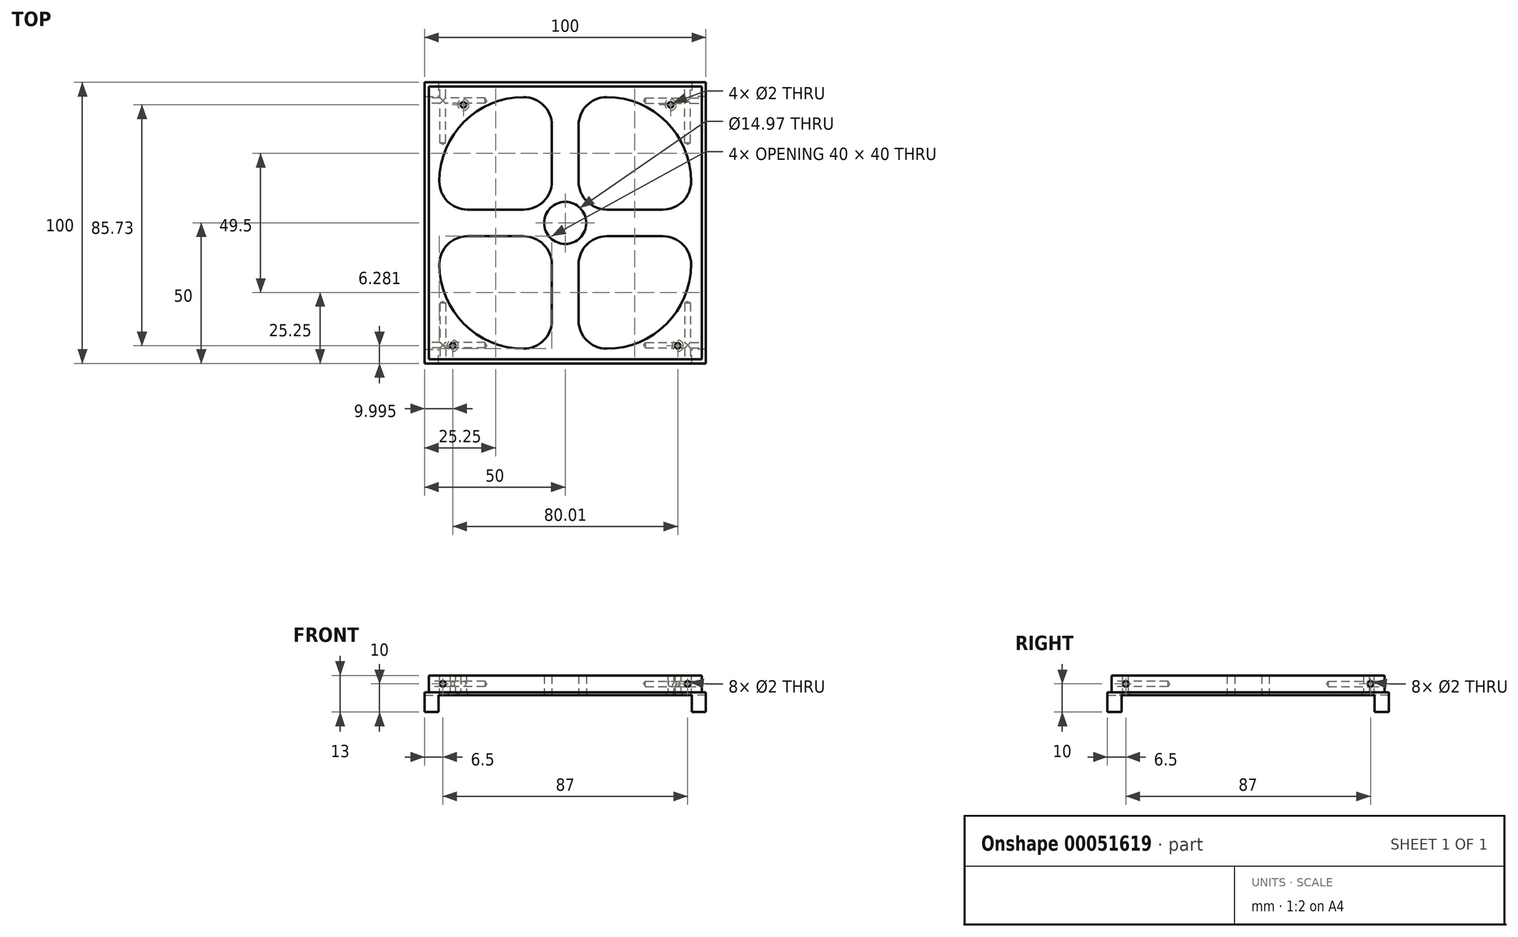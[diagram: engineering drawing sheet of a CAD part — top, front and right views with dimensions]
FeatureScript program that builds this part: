
annotation { "Feature Type Name" : "Feature", "Feature Type Description" : "" }
export const myFeature = defineFeature(function(context is Context, id is Id, definition is map)
    precondition{}
    {
        {
            var Q0;
            Q0=qCreatedBy(makeId("Top.planeOp"),FACE);
            var sketch = newSketch(context, id + "F0", { "sketchPlane" : qUnion([Q0])});
            skLineSegment(sketch, "E0.rect.bottom", {"start": v(-50, 50) * mm, "end": v(50, 50) * mm});
            skLineSegment(sketch, "E0.rect.top", {"start": v(-50, -50) * mm, "end": v(50, -50) * mm});
            skLineSegment(sketch, "E0.rect.left", {"start": v(-50, 50) * mm, "end": v(-50, -50) * mm});
            skLineSegment(sketch, "E0.rect.right", {"start": v(50, 50) * mm, "end": v(50, -50) * mm});
            skPoint(sketch, "E0.rect.middle", {"position": v(0, 0) * mm});
            skLineSegment(sketch, "E1.rect.bottom", {"start": v(-48.5, 48.5) * mm, "end": v(48.5, 48.5) * mm});
            skLineSegment(sketch, "E1.rect.top", {"start": v(-48.5, -48.5) * mm, "end": v(48.5, -48.5) * mm});
            skLineSegment(sketch, "E1.rect.left", {"start": v(-48.5, 48.5) * mm, "end": v(-48.5, -48.5) * mm});
            skLineSegment(sketch, "E1.rect.right", {"start": v(48.5, 48.5) * mm, "end": v(48.5, -48.5) * mm});
            skLineSegment(sketch, "E2.rect.bottom", {"start": v(-14.75, 4.75) * mm, "end": v(-34.75, 4.75) * mm});
            skLineSegment(sketch, "E2.rect.top", {"start": v(-14.75, 44.75) * mm, "end": v(-14.75, 44.75) * mm});
            skLineSegment(sketch, "E2.rect.left", {"start": v(-4.75, 14.75) * mm, "end": v(-4.75, 34.75) * mm});
            skLineSegment(sketch, "E2.rect.right", {"start": v(-44.75, 14.75) * mm, "end": v(-44.75, 14.75) * mm});
            skPoint(sketch, "E2.rect.middle", {"position": v(-24.75, 24.75) * mm});
            skPoint(sketch, "E3.visualSharp", {"position": v(-44.75, 44.75) * mm});
            skArc(sketch, "E3.filletArc", {"start": v(-14.75, 44.75) * mm, "mid": v(-35.96, 35.96) * mm, "end": v(-44.75, 14.75) * mm});
            skPoint(sketch, "E4.visualSharp", {"position": v(-4.75, 44.75) * mm});
            skArc(sketch, "E4.filletArc", {"start": v(-4.75, 34.75) * mm, "mid": v(-7.68, 41.82) * mm, "end": v(-14.75, 44.75) * mm});
            skPoint(sketch, "E5.visualSharp", {"position": v(-4.75, 4.75) * mm});
            skArc(sketch, "E5.filletArc", {"start": v(-14.75, 4.75) * mm, "mid": v(-7.68, 7.68) * mm, "end": v(-4.75, 14.75) * mm});
            skPoint(sketch, "E6.visualSharp", {"position": v(-44.75, 4.75) * mm});
            skArc(sketch, "E6.filletArc", {"start": v(-44.75, 14.75) * mm, "mid": v(-41.82, 7.68) * mm, "end": v(-34.75, 4.75) * mm});
            skLineSegment(sketch, "E7.MirrorCS", {"start": v(4.75, 14.75) * mm, "end": v(4.75, 34.75) * mm});
            skArc(sketch, "E8.MirrorCS", {"start": v(4.75, 34.75) * mm, "mid": v(7.68, 41.82) * mm, "end": v(14.75, 44.75) * mm});
            skLineSegment(sketch, "E9.MirrorCS", {"start": v(14.75, 44.75) * mm, "end": v(14.75, 44.75) * mm});
            skArc(sketch, "E10.MirrorCS", {"start": v(14.75, 44.75) * mm, "mid": v(35.96, 35.96) * mm, "end": v(44.75, 14.75) * mm});
            skLineSegment(sketch, "E11.MirrorCS", {"start": v(44.75, 14.75) * mm, "end": v(44.75, 14.75) * mm});
            skArc(sketch, "E12.MirrorCS", {"start": v(44.75, 14.75) * mm, "mid": v(41.82, 7.68) * mm, "end": v(34.75, 4.75) * mm});
            skLineSegment(sketch, "E13.MirrorCS", {"start": v(14.75, 4.75) * mm, "end": v(34.75, 4.75) * mm});
            skArc(sketch, "E14.MirrorCS", {"start": v(14.75, 4.75) * mm, "mid": v(7.68, 7.68) * mm, "end": v(4.75, 14.75) * mm});
            skPoint(sketch, "E15.MirrorP", {"position": v(24.75, 24.75) * mm});
            skArc(sketch, "E16.MirrorCS", {"start": v(14.75, -4.75) * mm, "mid": v(7.68, -7.68) * mm, "end": v(4.75, -14.75) * mm});
            skLineSegment(sketch, "E17.MirrorCS", {"start": v(4.75, -14.75) * mm, "end": v(4.75, -34.75) * mm});
            skArc(sketch, "E18.MirrorCS", {"start": v(4.75, -34.75) * mm, "mid": v(7.68, -41.82) * mm, "end": v(14.75, -44.75) * mm});
            skLineSegment(sketch, "E19.MirrorCS", {"start": v(14.75, -44.75) * mm, "end": v(14.75, -44.75) * mm});
            skArc(sketch, "E20.MirrorCS", {"start": v(14.75, -44.75) * mm, "mid": v(35.96, -35.96) * mm, "end": v(44.75, -14.75) * mm});
            skLineSegment(sketch, "E21.MirrorCS", {"start": v(44.75, -14.75) * mm, "end": v(44.75, -14.75) * mm});
            skArc(sketch, "E22.MirrorCS", {"start": v(44.75, -14.75) * mm, "mid": v(41.82, -7.68) * mm, "end": v(34.75, -4.75) * mm});
            skLineSegment(sketch, "E23.MirrorCS", {"start": v(14.75, -4.75) * mm, "end": v(34.75, -4.75) * mm});
            skPoint(sketch, "E24.MirrorP", {"position": v(24.75, -24.75) * mm});
            skLineSegment(sketch, "E25.MirrorCS", {"start": v(-4.75, -14.75) * mm, "end": v(-4.75, -34.75) * mm});
            skArc(sketch, "E26.MirrorCS", {"start": v(-14.75, -4.75) * mm, "mid": v(-7.68, -7.68) * mm, "end": v(-4.75, -14.75) * mm});
            skLineSegment(sketch, "E27.MirrorCS", {"start": v(-14.75, -4.75) * mm, "end": v(-34.75, -4.75) * mm});
            skArc(sketch, "E28.MirrorCS", {"start": v(-44.75, -14.75) * mm, "mid": v(-41.82, -7.68) * mm, "end": v(-34.75, -4.75) * mm});
            skLineSegment(sketch, "E29.MirrorCS", {"start": v(-44.75, -14.75) * mm, "end": v(-44.75, -14.75) * mm});
            skArc(sketch, "E30.MirrorCS", {"start": v(-14.75, -44.75) * mm, "mid": v(-35.96, -35.96) * mm, "end": v(-44.75, -14.75) * mm});
            skLineSegment(sketch, "E31.MirrorCS", {"start": v(-14.75, -44.75) * mm, "end": v(-14.75, -44.75) * mm});
            skArc(sketch, "E32.MirrorCS", {"start": v(-4.75, -34.75) * mm, "mid": v(-7.68, -41.82) * mm, "end": v(-14.75, -44.75) * mm});
            skPoint(sketch, "E33.MirrorP", {"position": v(-24.75, -24.75) * mm});
            skPoint(sketch, "E34", {"position": v(42.5, -42.5) * mm});
            skPoint(sketch, "E35.MirrorP", {"position": v(-42.5, -42.5) * mm});
            skPoint(sketch, "E36.MirrorP", {"position": v(42.5, 42.5) * mm});
            skPoint(sketch, "E37.MirrorP", {"position": v(-42.5, 42.5) * mm});
            skCircle(sketch, "E38", {"center": v(0, 0) * mm, "radius": 7.48 * mm});
            skSolve(sketch);
        }
        {
            var Q0;
            Q0=makeQuery(id+"F0.imprint","IMPRINT",FACE,{"disambiguationData":[TD([[makeQuery(id+"F0.imprint","IMPRINT",EDGE,{"derivedFrom":sQuery(id+"F0.wireOp",EDGE,"E1.rect.bottom")}),-1.0]])]});
            extrude(context, id + "F1", {"entities" : qUnion([Q0]), "depth" : 6 * mm});
        }
        {
            var Q0;
            Q0=qSketchRegion(id+"F0",true);
            var Q1;
            Q1=makeQuery(id+"F1.opExtrude","CAP_FACE",FACE,{"disambiguationData":[OSD([sQuery(id+"F0.wireOp",EDGE,"E1.rect.bottom"),sQuery(id+"F0.wireOp",EDGE,"E1.rect.top"),sQuery(id+"F0.wireOp",EDGE,"E1.rect.left"),sQuery(id+"F0.wireOp",EDGE,"E1.rect.right"),sQuery(id+"F0.wireOp",EDGE,"E2.rect.bottom"),sQuery(id+"F0.wireOp",EDGE,"E2.rect.top"),sQuery(id+"F0.wireOp",EDGE,"E2.rect.left"),sQuery(id+"F0.wireOp",EDGE,"E2.rect.right"),sQuery(id+"F0.wireOp",EDGE,"d764ca65-7f6a-4e13-98eb-a7907a3d072d0.MirrorCS"),sQuery(id+"F0.wireOp",EDGE,"4e8c5bec-c53d-4312-8259-349e49f543fe0.MirrorCS"),sQuery(id+"F0.wireOp",EDGE,"d6a0bf7c-e4bc-484e-b3d5-183d898144500.MirrorCS"),sQuery(id+"F0.wireOp",EDGE,"45a758ec-378c-46c5-b086-a70cc1cacffd0.MirrorCS"),sQuery(id+"F0.wireOp",EDGE,"a64d5360-d78c-41ef-9f44-8c8436a09bba0.MirrorCS"),sQuery(id+"F0.wireOp",EDGE,"c998a958-b69a-464e-a296-dd7f6d349ec80.MirrorCS"),sQuery(id+"F0.wireOp",EDGE,"a4bf1b2a-a2f4-4ab3-9d73-85797b196d270.MirrorCS"),sQuery(id+"F0.wireOp",EDGE,"ecd2f3fb-4ea3-4913-80f4-94ebebe2d04e0.MirrorCS"),sQuery(id+"F0.wireOp",EDGE,"085a2cb5-2e3f-4cc3-a5b9-01c6e75669f10.MirrorCS"),sQuery(id+"F0.wireOp",EDGE,"73d67a52-dadc-4bd6-8141-d25047cb753b0.MirrorCS"),sQuery(id+"F0.wireOp",EDGE,"8f6832c0-858d-4205-8574-29f35786d1620.MirrorCS"),sQuery(id+"F0.wireOp",EDGE,"ecc9a695-4792-4055-9804-abf58933c5b20.MirrorCS")])],"isStart":false});
            extrude(context, id + "F2", {"entities" : qUnion([Q0, Q1]), "operationType" : NewBodyOperationType.ADD, "depth" : 1 * mm});
        }
        {
            var Q0;
            {var subQ0=sQuery(id+"F0.wireOp",EDGE,"E1.rect.bottom");Q0=makeQuery(id+"F2.boolean.opBoolean","MERGE",FACE,{"derivedFrom":[makeQuery(id+"F1.opExtrude","SWEPT_FACE",FACE,{"disambiguationData":[OSD([subQ0])]}),makeQuery(id+"F2.opExtrude","SWEPT_FACE",FACE,{"disambiguationData":[OSD([subQ0]),TDD([makeQuery(id+"F1.opExtrude","CAP_EDGE",EDGE,{"disambiguationData":[OSD([subQ0])],"isStart":false})])]})]});}
            var sketch = newSketch(context, id + "F3", { "sketchPlane" : qUnion([Q0])});
            skPoint(sketch, "E39", {"position": v(-43.5, 4) * mm});
            skPoint(sketch, "E40.MirrorP", {"position": v(43.5, 4) * mm});
            skSolve(sketch);
        }
        {
            var Q0;
            Q0=sQuery(id+"F3.wireOp",VERTEX,"E39");
            var Q1;
            Q1=sQuery(id+"F3.wireOp",VERTEX,"E40.MirrorP");
            var Q2;
            Q2=makeQuery(id+"F1.opExtrude","SWEPT_BODY",BODY,{"disambiguationData":[OSD([sQuery(id+"F0.wireOp",EDGE,"E1.rect.bottom"),sQuery(id+"F0.wireOp",EDGE,"E1.rect.top"),sQuery(id+"F0.wireOp",EDGE,"E1.rect.left"),sQuery(id+"F0.wireOp",EDGE,"E1.rect.right"),sQuery(id+"F0.wireOp",EDGE,"E2.rect.bottom"),sQuery(id+"F0.wireOp",EDGE,"E2.rect.top"),sQuery(id+"F0.wireOp",EDGE,"E2.rect.left"),sQuery(id+"F0.wireOp",EDGE,"E2.rect.right"),sQuery(id+"F0.wireOp",EDGE,"E3.filletArc"),sQuery(id+"F0.wireOp",EDGE,"E4.filletArc"),sQuery(id+"F0.wireOp",EDGE,"E5.filletArc"),sQuery(id+"F0.wireOp",EDGE,"E6.filletArc"),sQuery(id+"F0.wireOp",EDGE,"E7.MirrorCS"),sQuery(id+"F0.wireOp",EDGE,"E8.MirrorCS"),sQuery(id+"F0.wireOp",EDGE,"E9.MirrorCS"),sQuery(id+"F0.wireOp",EDGE,"E10.MirrorCS"),sQuery(id+"F0.wireOp",EDGE,"E11.MirrorCS"),sQuery(id+"F0.wireOp",EDGE,"E12.MirrorCS"),sQuery(id+"F0.wireOp",EDGE,"E13.MirrorCS"),sQuery(id+"F0.wireOp",EDGE,"E14.MirrorCS"),sQuery(id+"F0.wireOp",EDGE,"E16.MirrorCS"),sQuery(id+"F0.wireOp",EDGE,"E17.MirrorCS"),sQuery(id+"F0.wireOp",EDGE,"E18.MirrorCS"),sQuery(id+"F0.wireOp",EDGE,"E19.MirrorCS"),sQuery(id+"F0.wireOp",EDGE,"E20.MirrorCS"),sQuery(id+"F0.wireOp",EDGE,"E21.MirrorCS"),sQuery(id+"F0.wireOp",EDGE,"E22.MirrorCS"),sQuery(id+"F0.wireOp",EDGE,"E23.MirrorCS"),sQuery(id+"F0.wireOp",EDGE,"E25.MirrorCS"),sQuery(id+"F0.wireOp",EDGE,"E26.MirrorCS"),sQuery(id+"F0.wireOp",EDGE,"E27.MirrorCS"),sQuery(id+"F0.wireOp",EDGE,"E28.MirrorCS"),sQuery(id+"F0.wireOp",EDGE,"E29.MirrorCS"),sQuery(id+"F0.wireOp",EDGE,"E30.MirrorCS"),sQuery(id+"F0.wireOp",EDGE,"E31.MirrorCS"),sQuery(id+"F0.wireOp",EDGE,"E32.MirrorCS")])]});
            hole(context, id + "F4", {"style" : HoleStyle.SIMPLE, "holeDiameter" : 2 * mm, "endStyle" : HoleEndStyle.BLIND, "holeDepth" : 20 * mm, "locations" : qUnion([Q0, Q1]), "scope" : qUnion([Q2])});
        }
        {
            var Q0;
            {var subQ0=sQuery(id+"F0.wireOp",EDGE,"E1.rect.left");Q0=makeQuery(id+"F2.boolean.opBoolean","MERGE",FACE,{"derivedFrom":[makeQuery(id+"F1.opExtrude","SWEPT_FACE",FACE,{"disambiguationData":[OSD([subQ0])]}),makeQuery(id+"F2.opExtrude","SWEPT_FACE",FACE,{"disambiguationData":[OSD([subQ0]),TDD([makeQuery(id+"F1.opExtrude","CAP_EDGE",EDGE,{"disambiguationData":[OSD([subQ0])],"isStart":false})])]})]});}
            var sketch = newSketch(context, id + "F5", { "sketchPlane" : qUnion([Q0])});
            skPoint(sketch, "E41", {"position": v(-43.5, 4) * mm});
            skPoint(sketch, "E42.MirrorP", {"position": v(43.5, 4) * mm});
            skSolve(sketch);
        }
        {
            var Q0;
            Q0=sQuery(id+"F5.wireOp",VERTEX,"E41");
            var Q1;
            Q1=sQuery(id+"F5.wireOp",VERTEX,"E42.MirrorP");
            var Q2;
            Q2=makeQuery(id+"F1.opExtrude","SWEPT_BODY",BODY,{"disambiguationData":[OSD([sQuery(id+"F0.wireOp",EDGE,"E1.rect.bottom"),sQuery(id+"F0.wireOp",EDGE,"E1.rect.top"),sQuery(id+"F0.wireOp",EDGE,"E1.rect.left"),sQuery(id+"F0.wireOp",EDGE,"E1.rect.right"),sQuery(id+"F0.wireOp",EDGE,"E2.rect.bottom"),sQuery(id+"F0.wireOp",EDGE,"E2.rect.top"),sQuery(id+"F0.wireOp",EDGE,"E2.rect.left"),sQuery(id+"F0.wireOp",EDGE,"E2.rect.right"),sQuery(id+"F0.wireOp",EDGE,"E3.filletArc"),sQuery(id+"F0.wireOp",EDGE,"E4.filletArc"),sQuery(id+"F0.wireOp",EDGE,"E5.filletArc"),sQuery(id+"F0.wireOp",EDGE,"E6.filletArc"),sQuery(id+"F0.wireOp",EDGE,"E7.MirrorCS"),sQuery(id+"F0.wireOp",EDGE,"E8.MirrorCS"),sQuery(id+"F0.wireOp",EDGE,"E9.MirrorCS"),sQuery(id+"F0.wireOp",EDGE,"E10.MirrorCS"),sQuery(id+"F0.wireOp",EDGE,"E11.MirrorCS"),sQuery(id+"F0.wireOp",EDGE,"E12.MirrorCS"),sQuery(id+"F0.wireOp",EDGE,"E13.MirrorCS"),sQuery(id+"F0.wireOp",EDGE,"E14.MirrorCS"),sQuery(id+"F0.wireOp",EDGE,"E16.MirrorCS"),sQuery(id+"F0.wireOp",EDGE,"E17.MirrorCS"),sQuery(id+"F0.wireOp",EDGE,"E18.MirrorCS"),sQuery(id+"F0.wireOp",EDGE,"E19.MirrorCS"),sQuery(id+"F0.wireOp",EDGE,"E20.MirrorCS"),sQuery(id+"F0.wireOp",EDGE,"E21.MirrorCS"),sQuery(id+"F0.wireOp",EDGE,"E22.MirrorCS"),sQuery(id+"F0.wireOp",EDGE,"E23.MirrorCS"),sQuery(id+"F0.wireOp",EDGE,"E25.MirrorCS"),sQuery(id+"F0.wireOp",EDGE,"E26.MirrorCS"),sQuery(id+"F0.wireOp",EDGE,"E27.MirrorCS"),sQuery(id+"F0.wireOp",EDGE,"E28.MirrorCS"),sQuery(id+"F0.wireOp",EDGE,"E29.MirrorCS"),sQuery(id+"F0.wireOp",EDGE,"E30.MirrorCS"),sQuery(id+"F0.wireOp",EDGE,"E31.MirrorCS"),sQuery(id+"F0.wireOp",EDGE,"E32.MirrorCS")])]});
            hole(context, id + "F6", {"style" : HoleStyle.SIMPLE, "holeDiameter" : 2 * mm, "endStyle" : HoleEndStyle.BLIND, "holeDepth" : 20 * mm, "locations" : qUnion([Q0, Q1]), "scope" : qUnion([Q2])});
        }
        {
            var Q0;
            {var subQ0=sQuery(id+"F0.wireOp",EDGE,"E1.rect.top");Q0=makeQuery(id+"F2.boolean.opBoolean","MERGE",FACE,{"derivedFrom":[makeQuery(id+"F1.opExtrude","SWEPT_FACE",FACE,{"disambiguationData":[OSD([subQ0])]}),makeQuery(id+"F2.opExtrude","SWEPT_FACE",FACE,{"disambiguationData":[OSD([subQ0]),TDD([makeQuery(id+"F1.opExtrude","CAP_EDGE",EDGE,{"disambiguationData":[OSD([subQ0])],"isStart":false})])]})]});}
            var sketch = newSketch(context, id + "F7", { "sketchPlane" : qUnion([Q0])});
            skPoint(sketch, "E43", {"position": v(-43.5, 4) * mm});
            skPoint(sketch, "E44.MirrorP", {"position": v(43.5, 4) * mm});
            skSolve(sketch);
        }
        {
            var Q0;
            Q0=sQuery(id+"F7.wireOp",VERTEX,"E43");
            var Q1;
            Q1=sQuery(id+"F7.wireOp",VERTEX,"E44.MirrorP");
            var Q2;
            Q2=makeQuery(id+"F1.opExtrude","SWEPT_BODY",BODY,{"disambiguationData":[OSD([sQuery(id+"F0.wireOp",EDGE,"E1.rect.bottom"),sQuery(id+"F0.wireOp",EDGE,"E1.rect.top"),sQuery(id+"F0.wireOp",EDGE,"E1.rect.left"),sQuery(id+"F0.wireOp",EDGE,"E1.rect.right"),sQuery(id+"F0.wireOp",EDGE,"E2.rect.bottom"),sQuery(id+"F0.wireOp",EDGE,"E2.rect.top"),sQuery(id+"F0.wireOp",EDGE,"E2.rect.left"),sQuery(id+"F0.wireOp",EDGE,"E2.rect.right"),sQuery(id+"F0.wireOp",EDGE,"E3.filletArc"),sQuery(id+"F0.wireOp",EDGE,"E4.filletArc"),sQuery(id+"F0.wireOp",EDGE,"E5.filletArc"),sQuery(id+"F0.wireOp",EDGE,"E6.filletArc"),sQuery(id+"F0.wireOp",EDGE,"E7.MirrorCS"),sQuery(id+"F0.wireOp",EDGE,"E8.MirrorCS"),sQuery(id+"F0.wireOp",EDGE,"E9.MirrorCS"),sQuery(id+"F0.wireOp",EDGE,"E10.MirrorCS"),sQuery(id+"F0.wireOp",EDGE,"E11.MirrorCS"),sQuery(id+"F0.wireOp",EDGE,"E12.MirrorCS"),sQuery(id+"F0.wireOp",EDGE,"E13.MirrorCS"),sQuery(id+"F0.wireOp",EDGE,"E14.MirrorCS"),sQuery(id+"F0.wireOp",EDGE,"E16.MirrorCS"),sQuery(id+"F0.wireOp",EDGE,"E17.MirrorCS"),sQuery(id+"F0.wireOp",EDGE,"E18.MirrorCS"),sQuery(id+"F0.wireOp",EDGE,"E19.MirrorCS"),sQuery(id+"F0.wireOp",EDGE,"E20.MirrorCS"),sQuery(id+"F0.wireOp",EDGE,"E21.MirrorCS"),sQuery(id+"F0.wireOp",EDGE,"E22.MirrorCS"),sQuery(id+"F0.wireOp",EDGE,"E23.MirrorCS"),sQuery(id+"F0.wireOp",EDGE,"E25.MirrorCS"),sQuery(id+"F0.wireOp",EDGE,"E26.MirrorCS"),sQuery(id+"F0.wireOp",EDGE,"E27.MirrorCS"),sQuery(id+"F0.wireOp",EDGE,"E28.MirrorCS"),sQuery(id+"F0.wireOp",EDGE,"E29.MirrorCS"),sQuery(id+"F0.wireOp",EDGE,"E30.MirrorCS"),sQuery(id+"F0.wireOp",EDGE,"E31.MirrorCS"),sQuery(id+"F0.wireOp",EDGE,"E32.MirrorCS")])]});
            hole(context, id + "F8", {"style" : HoleStyle.SIMPLE, "holeDiameter" : 2 * mm, "endStyle" : HoleEndStyle.BLIND, "holeDepth" : 20 * mm, "locations" : qUnion([Q0, Q1]), "scope" : qUnion([Q2])});
        }
        {
            var Q0;
            {var subQ0=sQuery(id+"F0.wireOp",EDGE,"E1.rect.right");Q0=makeQuery(id+"F2.boolean.opBoolean","MERGE",FACE,{"derivedFrom":[makeQuery(id+"F1.opExtrude","SWEPT_FACE",FACE,{"disambiguationData":[OSD([subQ0])]}),makeQuery(id+"F2.opExtrude","SWEPT_FACE",FACE,{"disambiguationData":[OSD([subQ0]),TDD([makeQuery(id+"F1.opExtrude","CAP_EDGE",EDGE,{"disambiguationData":[OSD([subQ0])],"isStart":false})])]})]});}
            var sketch = newSketch(context, id + "F9", { "sketchPlane" : qUnion([Q0])});
            skPoint(sketch, "E45", {"position": v(-43.5, 4) * mm});
            skPoint(sketch, "E46.MirrorP", {"position": v(43.5, 4) * mm});
            skSolve(sketch);
        }
        {
            var Q0;
            Q0=sQuery(id+"F9.wireOp",VERTEX,"E45");
            var Q1;
            Q1=sQuery(id+"F9.wireOp",VERTEX,"E46.MirrorP");
            var Q2;
            Q2=makeQuery(id+"F1.opExtrude","SWEPT_BODY",BODY,{"disambiguationData":[OSD([sQuery(id+"F0.wireOp",EDGE,"E1.rect.bottom"),sQuery(id+"F0.wireOp",EDGE,"E1.rect.top"),sQuery(id+"F0.wireOp",EDGE,"E1.rect.left"),sQuery(id+"F0.wireOp",EDGE,"E1.rect.right"),sQuery(id+"F0.wireOp",EDGE,"E2.rect.bottom"),sQuery(id+"F0.wireOp",EDGE,"E2.rect.top"),sQuery(id+"F0.wireOp",EDGE,"E2.rect.left"),sQuery(id+"F0.wireOp",EDGE,"E2.rect.right"),sQuery(id+"F0.wireOp",EDGE,"E3.filletArc"),sQuery(id+"F0.wireOp",EDGE,"E4.filletArc"),sQuery(id+"F0.wireOp",EDGE,"E5.filletArc"),sQuery(id+"F0.wireOp",EDGE,"E6.filletArc"),sQuery(id+"F0.wireOp",EDGE,"E7.MirrorCS"),sQuery(id+"F0.wireOp",EDGE,"E8.MirrorCS"),sQuery(id+"F0.wireOp",EDGE,"E9.MirrorCS"),sQuery(id+"F0.wireOp",EDGE,"E10.MirrorCS"),sQuery(id+"F0.wireOp",EDGE,"E11.MirrorCS"),sQuery(id+"F0.wireOp",EDGE,"E12.MirrorCS"),sQuery(id+"F0.wireOp",EDGE,"E13.MirrorCS"),sQuery(id+"F0.wireOp",EDGE,"E14.MirrorCS"),sQuery(id+"F0.wireOp",EDGE,"E16.MirrorCS"),sQuery(id+"F0.wireOp",EDGE,"E17.MirrorCS"),sQuery(id+"F0.wireOp",EDGE,"E18.MirrorCS"),sQuery(id+"F0.wireOp",EDGE,"E19.MirrorCS"),sQuery(id+"F0.wireOp",EDGE,"E20.MirrorCS"),sQuery(id+"F0.wireOp",EDGE,"E21.MirrorCS"),sQuery(id+"F0.wireOp",EDGE,"E22.MirrorCS"),sQuery(id+"F0.wireOp",EDGE,"E23.MirrorCS"),sQuery(id+"F0.wireOp",EDGE,"E25.MirrorCS"),sQuery(id+"F0.wireOp",EDGE,"E26.MirrorCS"),sQuery(id+"F0.wireOp",EDGE,"E27.MirrorCS"),sQuery(id+"F0.wireOp",EDGE,"E28.MirrorCS"),sQuery(id+"F0.wireOp",EDGE,"E29.MirrorCS"),sQuery(id+"F0.wireOp",EDGE,"E30.MirrorCS"),sQuery(id+"F0.wireOp",EDGE,"E31.MirrorCS"),sQuery(id+"F0.wireOp",EDGE,"E32.MirrorCS")])]});
            hole(context, id + "F10", {"style" : HoleStyle.SIMPLE, "holeDiameter" : 2 * mm, "endStyle" : HoleEndStyle.BLIND, "holeDepth" : 20 * mm, "locations" : qUnion([Q0, Q1]), "scope" : qUnion([Q2])});
        }
        {
            var Q0;
            {var subQ0=sQuery(id+"F0.wireOp",EDGE,"E1.rect.bottom");var subQ1=sQuery(id+"F0.wireOp",EDGE,"E1.rect.top");var subQ2=sQuery(id+"F0.wireOp",EDGE,"E1.rect.left");var subQ3=sQuery(id+"F0.wireOp",EDGE,"E1.rect.right");Q0=makeQuery(id+"F2.boolean.opBoolean","MERGE",FACE,{"derivedFrom":[makeQuery(id+"F1.opExtrude","CAP_FACE",FACE,{"disambiguationData":[OSD([subQ0,subQ1,subQ2,subQ3,sQuery(id+"F0.wireOp",EDGE,"E2.rect.bottom"),sQuery(id+"F0.wireOp",EDGE,"E2.rect.top"),sQuery(id+"F0.wireOp",EDGE,"E2.rect.left"),sQuery(id+"F0.wireOp",EDGE,"E2.rect.right"),sQuery(id+"F0.wireOp",EDGE,"E3.filletArc"),sQuery(id+"F0.wireOp",EDGE,"E4.filletArc"),sQuery(id+"F0.wireOp",EDGE,"E5.filletArc"),sQuery(id+"F0.wireOp",EDGE,"E6.filletArc"),sQuery(id+"F0.wireOp",EDGE,"E7.MirrorCS"),sQuery(id+"F0.wireOp",EDGE,"E8.MirrorCS"),sQuery(id+"F0.wireOp",EDGE,"E9.MirrorCS"),sQuery(id+"F0.wireOp",EDGE,"E10.MirrorCS"),sQuery(id+"F0.wireOp",EDGE,"E11.MirrorCS"),sQuery(id+"F0.wireOp",EDGE,"E12.MirrorCS"),sQuery(id+"F0.wireOp",EDGE,"E13.MirrorCS"),sQuery(id+"F0.wireOp",EDGE,"E14.MirrorCS"),sQuery(id+"F0.wireOp",EDGE,"E16.MirrorCS"),sQuery(id+"F0.wireOp",EDGE,"E17.MirrorCS"),sQuery(id+"F0.wireOp",EDGE,"E18.MirrorCS"),sQuery(id+"F0.wireOp",EDGE,"E19.MirrorCS"),sQuery(id+"F0.wireOp",EDGE,"E20.MirrorCS"),sQuery(id+"F0.wireOp",EDGE,"E21.MirrorCS"),sQuery(id+"F0.wireOp",EDGE,"E22.MirrorCS"),sQuery(id+"F0.wireOp",EDGE,"E23.MirrorCS"),sQuery(id+"F0.wireOp",EDGE,"E25.MirrorCS"),sQuery(id+"F0.wireOp",EDGE,"E26.MirrorCS"),sQuery(id+"F0.wireOp",EDGE,"E27.MirrorCS"),sQuery(id+"F0.wireOp",EDGE,"E28.MirrorCS"),sQuery(id+"F0.wireOp",EDGE,"E29.MirrorCS"),sQuery(id+"F0.wireOp",EDGE,"E30.MirrorCS"),sQuery(id+"F0.wireOp",EDGE,"E31.MirrorCS"),sQuery(id+"F0.wireOp",EDGE,"E32.MirrorCS")])],"isStart":true}),makeQuery(id+"F2.opExtrude","CAP_FACE",FACE,{"disambiguationData":[OSD([sQuery(id+"F0.wireOp",EDGE,"E0.rect.bottom"),sQuery(id+"F0.wireOp",EDGE,"E0.rect.top"),sQuery(id+"F0.wireOp",EDGE,"E0.rect.left"),sQuery(id+"F0.wireOp",EDGE,"E0.rect.right"),subQ0,subQ1,subQ2,subQ3])],"isStart":true})]});}
            var sketch = newSketch(context, id + "F11", { "sketchPlane" : qUnion([Q0])});
            skPoint(sketch, "E47", {"position": v(-36.2, -42.01) * mm});
            skPoint(sketch, "E48", {"position": v(40, 43.72) * mm});
            skPoint(sketch, "E49", {"position": v(37.47, -42.01) * mm});
            skPoint(sketch, "E50", {"position": v(-40, 43.72) * mm});
            skLineSegment(sketch, "E51.bottom", {"start": v(50, -50) * mm, "end": v(45, -50) * mm});
            skLineSegment(sketch, "E51.top", {"start": v(50, -45) * mm, "end": v(45, -45) * mm});
            skLineSegment(sketch, "E51.left", {"start": v(50, -50) * mm, "end": v(50, -45) * mm});
            skLineSegment(sketch, "E51.right", {"start": v(45, -50) * mm, "end": v(45, -45) * mm});
            skLineSegment(sketch, "E52.MirrorCS", {"start": v(-50, -50) * mm, "end": v(-50, -45) * mm});
            skLineSegment(sketch, "E53.MirrorCS", {"start": v(-45, -50) * mm, "end": v(-45, -45) * mm});
            skLineSegment(sketch, "E54.MirrorCS", {"start": v(-50, -45) * mm, "end": v(-45, -45) * mm});
            skLineSegment(sketch, "E55.MirrorCS", {"start": v(-50, -50) * mm, "end": v(-45, -50) * mm});
            skLineSegment(sketch, "E56.MirrorCS", {"start": v(-50, 50) * mm, "end": v(-45, 50) * mm});
            skLineSegment(sketch, "E57.MirrorCS", {"start": v(-50, 45) * mm, "end": v(-45, 45) * mm});
            skLineSegment(sketch, "E58.MirrorCS", {"start": v(-50, 50) * mm, "end": v(-50, 45) * mm});
            skLineSegment(sketch, "E59.MirrorCS", {"start": v(-45, 50) * mm, "end": v(-45, 45) * mm});
            skLineSegment(sketch, "E60.MirrorCS", {"start": v(50, 50) * mm, "end": v(45, 50) * mm});
            skLineSegment(sketch, "E61.MirrorCS", {"start": v(50, 45) * mm, "end": v(45, 45) * mm});
            skLineSegment(sketch, "E62.MirrorCS", {"start": v(50, 50) * mm, "end": v(50, 45) * mm});
            skLineSegment(sketch, "E63.MirrorCS", {"start": v(45, 50) * mm, "end": v(45, 45) * mm});
            skSolve(sketch);
        }
        {
            var Q0;
            Q0=sQuery(id+"F11.wireOp",VERTEX,"E47");
            var Q1;
            Q1=sQuery(id+"F11.wireOp",VERTEX,"E50");
            var Q2;
            Q2=sQuery(id+"F11.wireOp",VERTEX,"E48");
            var Q3;
            Q3=sQuery(id+"F11.wireOp",VERTEX,"E49");
            var Q4;
            Q4=makeQuery(id+"F1.opExtrude","SWEPT_BODY",BODY,{"disambiguationData":[OSD([sQuery(id+"F0.wireOp",EDGE,"E1.rect.bottom"),sQuery(id+"F0.wireOp",EDGE,"E1.rect.top"),sQuery(id+"F0.wireOp",EDGE,"E1.rect.left"),sQuery(id+"F0.wireOp",EDGE,"E1.rect.right"),sQuery(id+"F0.wireOp",EDGE,"E2.rect.bottom"),sQuery(id+"F0.wireOp",EDGE,"E2.rect.top"),sQuery(id+"F0.wireOp",EDGE,"E2.rect.left"),sQuery(id+"F0.wireOp",EDGE,"E2.rect.right"),sQuery(id+"F0.wireOp",EDGE,"E3.filletArc"),sQuery(id+"F0.wireOp",EDGE,"E4.filletArc"),sQuery(id+"F0.wireOp",EDGE,"E5.filletArc"),sQuery(id+"F0.wireOp",EDGE,"E6.filletArc"),sQuery(id+"F0.wireOp",EDGE,"E7.MirrorCS"),sQuery(id+"F0.wireOp",EDGE,"E8.MirrorCS"),sQuery(id+"F0.wireOp",EDGE,"E9.MirrorCS"),sQuery(id+"F0.wireOp",EDGE,"E10.MirrorCS"),sQuery(id+"F0.wireOp",EDGE,"E11.MirrorCS"),sQuery(id+"F0.wireOp",EDGE,"E12.MirrorCS"),sQuery(id+"F0.wireOp",EDGE,"E13.MirrorCS"),sQuery(id+"F0.wireOp",EDGE,"E14.MirrorCS"),sQuery(id+"F0.wireOp",EDGE,"E16.MirrorCS"),sQuery(id+"F0.wireOp",EDGE,"E17.MirrorCS"),sQuery(id+"F0.wireOp",EDGE,"E18.MirrorCS"),sQuery(id+"F0.wireOp",EDGE,"E19.MirrorCS"),sQuery(id+"F0.wireOp",EDGE,"E20.MirrorCS"),sQuery(id+"F0.wireOp",EDGE,"E21.MirrorCS"),sQuery(id+"F0.wireOp",EDGE,"E22.MirrorCS"),sQuery(id+"F0.wireOp",EDGE,"E23.MirrorCS"),sQuery(id+"F0.wireOp",EDGE,"E25.MirrorCS"),sQuery(id+"F0.wireOp",EDGE,"E26.MirrorCS"),sQuery(id+"F0.wireOp",EDGE,"E27.MirrorCS"),sQuery(id+"F0.wireOp",EDGE,"E28.MirrorCS"),sQuery(id+"F0.wireOp",EDGE,"E29.MirrorCS"),sQuery(id+"F0.wireOp",EDGE,"E30.MirrorCS"),sQuery(id+"F0.wireOp",EDGE,"E31.MirrorCS"),sQuery(id+"F0.wireOp",EDGE,"E32.MirrorCS")])]});
            hole(context, id + "F12", {"style" : HoleStyle.C_SINK, "holeDiameter" : 2 * mm, "cSinkDiameter" : 4 * mm, "endStyle" : HoleEndStyle.THROUGH, "locations" : qUnion([Q0, Q1, Q2, Q3]), "scope" : qUnion([Q4]), "cSinkAngle" : 90 * degree});
        }
        {
            var Q0;
            Q0=makeQuery(id+"F11.imprint","IMPRINT",FACE,{"disambiguationData":[TD([[makeQuery(id+"F11.imprint","IMPRINT",EDGE,{"derivedFrom":sQuery(id+"F11.wireOp",EDGE,"E56.MirrorCS")}),-1.0]])]});
            var Q1;
            Q1=makeQuery(id+"F11.imprint","IMPRINT",FACE,{"disambiguationData":[TD([[makeQuery(id+"F11.imprint","IMPRINT",EDGE,{"derivedFrom":sQuery(id+"F11.wireOp",EDGE,"E60.MirrorCS")}),-1.0]])]});
            var Q2;
            Q2=makeQuery(id+"F11.imprint","IMPRINT",FACE,{"disambiguationData":[TD([[makeQuery(id+"F11.imprint","IMPRINT",EDGE,{"derivedFrom":sQuery(id+"F11.wireOp",EDGE,"E51.bottom")}),1.0]])]});
            var Q3;
            Q3=makeQuery(id+"F11.imprint","IMPRINT",FACE,{"disambiguationData":[TD([[makeQuery(id+"F11.imprint","IMPRINT",EDGE,{"derivedFrom":sQuery(id+"F11.wireOp",EDGE,"E52.MirrorCS")}),-1.0]])]});
            extrude(context, id + "F13", {"entities" : qUnion([Q0, Q1, Q2, Q3]), "operationType" : NewBodyOperationType.ADD, "depth" : 6 * mm});
        }
    });
